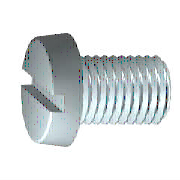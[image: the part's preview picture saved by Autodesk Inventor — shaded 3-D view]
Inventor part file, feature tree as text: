
AUTODESK INVENTOR PART (.ipt)
format: ipt  version: 2023.2 (Build 272271030, 271C)  size: 182,272 bytes
history: native  units: mm (DEFAULTED — no unit token found)
features: sketch x2, extrude x1, plane x1
ambient origin geometry x7: Origin, YZ Plane, XZ Plane, X Axis, Y Axis, Z Axis, Center Point
bodies: Solid1 (feature_tree), Body (feature_tree)
feature tree (4):
  sketch  "Sketch2"  dims[d2=0.49086mm d3=3.3mm d4=5.0mm d5=4.566987mm d8=90.0deg d7=0.0mm d9=8.5mm d10=0.872665mm d11=1.2mm d12=8.5mm d14=0.2mm d15=18.4mm d16=0.0mm d17=0.433015mm d18=0.49086mm d19=1.3mm d20=0.0mm d36=45.0deg d37=0.0mm d39=0.0mm]
  extrude  "Slot"  Depth=18.4mm
  plane  "Work Plane1"
  sketch  "Sketch1"  dims[d0=20.0mm d1=18.4mm]
